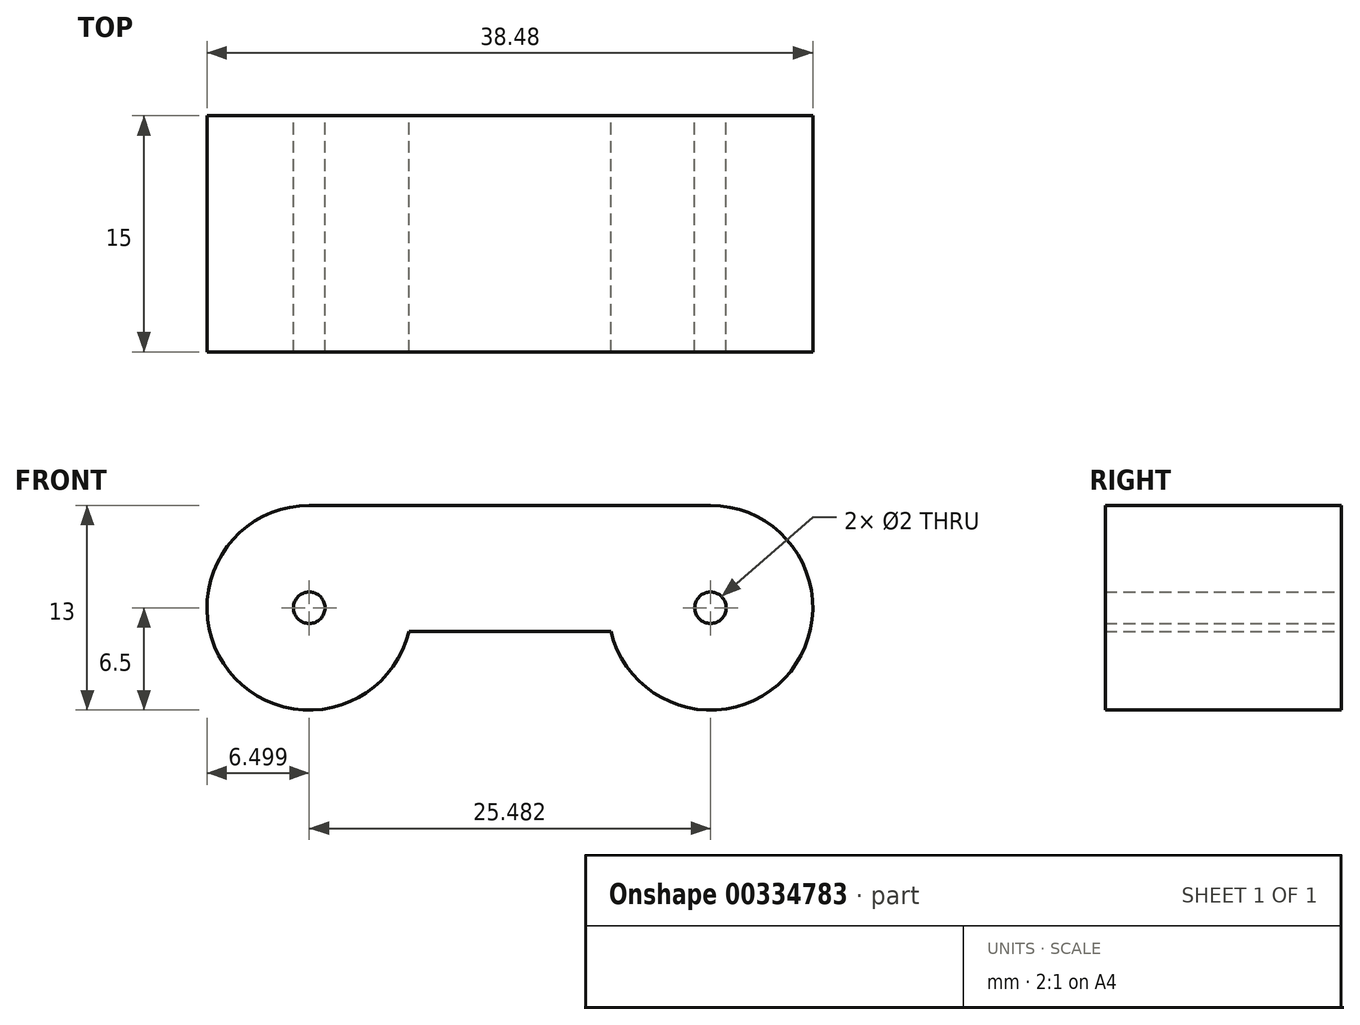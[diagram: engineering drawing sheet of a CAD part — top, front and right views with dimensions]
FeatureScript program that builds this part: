
annotation { "Feature Type Name" : "Feature", "Feature Type Description" : "" }
export const myFeature = defineFeature(function(context is Context, id is Id, definition is map)
    precondition{}
    {
        {
            var Q0;
            Q0=qCreatedBy(makeId("Front.planeOp"),FACE);
            var sketch = newSketch(context, id + "F0", { "sketchPlane" : qUnion([Q0])});
            skArc(sketch, "E0", {"start": v(-12.74, 6.5) * mm, "mid": v(-17.84, -4.03) * mm, "end": v(-6.42, -1.5) * mm});
            skArc(sketch, "E1.MirrorC", {"start": v(12.74, 6.5) * mm, "mid": v(17.84, -4.03) * mm, "end": v(6.42, -1.5) * mm});
            skLineSegment(sketch, "E2.bottom", {"start": v(-12.74, 6.5) * mm, "end": v(12.74, 6.5) * mm});
            skLineSegment(sketch, "E2.top", {"start": v(-6.42, -1.5) * mm, "end": v(6.42, -1.5) * mm});
            skPoint(sketch, "E3.orphan", {"position": v(12.74, -1.5) * mm});
            skCircle(sketch, "E4", {"center": v(-12.74, 0) * mm, "radius": 1 * mm});
            skCircle(sketch, "E5.MirrorC", {"center": v(12.74, 0) * mm, "radius": 1 * mm});
            skSolve(sketch);
        }
        {
            var Q0;
            Q0=makeQuery(id+"F0.imprint","IMPRINT",FACE,{"disambiguationData":[TD([[makeQuery(id+"F0.imprint","IMPRINT",EDGE,{"derivedFrom":sQuery(id+"F0.wireOp",EDGE,"E0")}),1.0]])]});
            extrude(context, id + "F1", {"entities" : qUnion([Q0]), "endBound" : BoundingType.SYMMETRIC, "depth" : 15 * mm});
        }
    });
